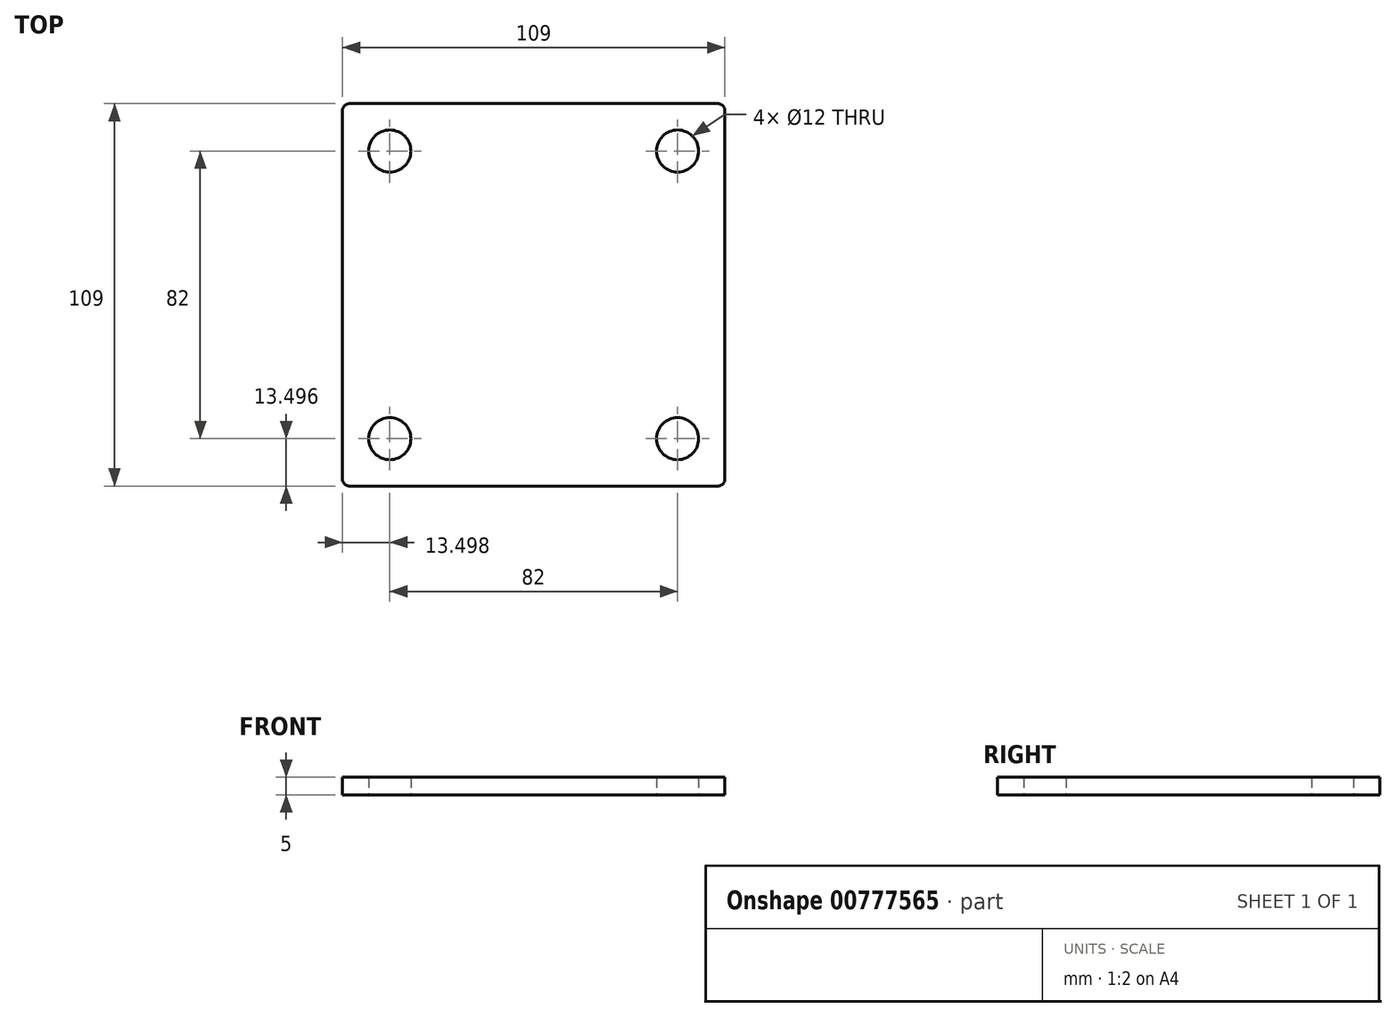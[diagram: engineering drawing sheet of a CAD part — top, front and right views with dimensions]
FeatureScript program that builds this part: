
annotation { "Feature Type Name" : "Feature", "Feature Type Description" : "" }
export const myFeature = defineFeature(function(context is Context, id is Id, definition is map)
    precondition{}
    {
        {
            var Q0;
            Q0=qCreatedBy(makeId("Top.planeOp"), FACE);
            var sketch = newSketch(context, id + "F0", { "sketchPlane" : qUnion([Q0])});
            skLineSegment(sketch, "E0.bottom", {"start": v(8.37, 84.5) * mm, "end": v(-96.63, 84.5) * mm});
            skLineSegment(sketch, "E0.top", {"start": v(8.37, -24.5) * mm, "end": v(-96.63, -24.5) * mm});
            skLineSegment(sketch, "E0.left", {"start": v(10.37, 82.5) * mm, "end": v(10.37, -22.5) * mm});
            skLineSegment(sketch, "E0.right", {"start": v(-98.63, 82.5) * mm, "end": v(-98.63, -22.5) * mm});
            skPoint(sketch, "E1.visualSharp", {"position": v(-98.63, 84.5) * mm});
            skArc(sketch, "E1.filletArc", {"start": v(-96.63, 84.5) * mm, "mid": v(-98.05, 83.92) * mm, "end": v(-98.63, 82.5) * mm});
            skPoint(sketch, "E2.visualSharp", {"position": v(-98.63, -24.5) * mm});
            skArc(sketch, "E2.filletArc", {"start": v(-98.63, -22.5) * mm, "mid": v(-98.05, -23.9) * mm, "end": v(-96.63, -24.5) * mm});
            skPoint(sketch, "E3.visualSharp", {"position": v(10.37, -24.5) * mm});
            skArc(sketch, "E3.filletArc", {"start": v(8.37, -24.5) * mm, "mid": v(9.78, -23.9) * mm, "end": v(10.37, -22.5) * mm});
            skPoint(sketch, "E4.visualSharp", {"position": v(10.37, 84.5) * mm});
            skArc(sketch, "E4.filletArc", {"start": v(10.37, 82.5) * mm, "mid": v(9.78, 83.92) * mm, "end": v(8.37, 84.5) * mm});
            skCircle(sketch, "E5", {"center": v(-3.13, 71) * mm, "radius": 6 * mm});
            skCircle(sketch, "E6", {"center": v(-85.13, -11) * mm, "radius": 6 * mm});
            skCircle(sketch, "E7", {"center": v(-85.13, 71) * mm, "radius": 6 * mm});
            skCircle(sketch, "E8", {"center": v(-3.13, -11) * mm, "radius": 6 * mm});
            skSolve(sketch);
        }
        {
            var Q0;
            Q0 = qSketchRegion(id + "F0", true);
            extrude(context, id + "F1", {"entities" : qUnion([Q0]), "flatOperationType" : FlatOperationType.REMOVE, "depth" : 5 * mm, "offsetDistance" : 25 * mm, "domain" : OperationDomain.MODEL});
        }
    });
